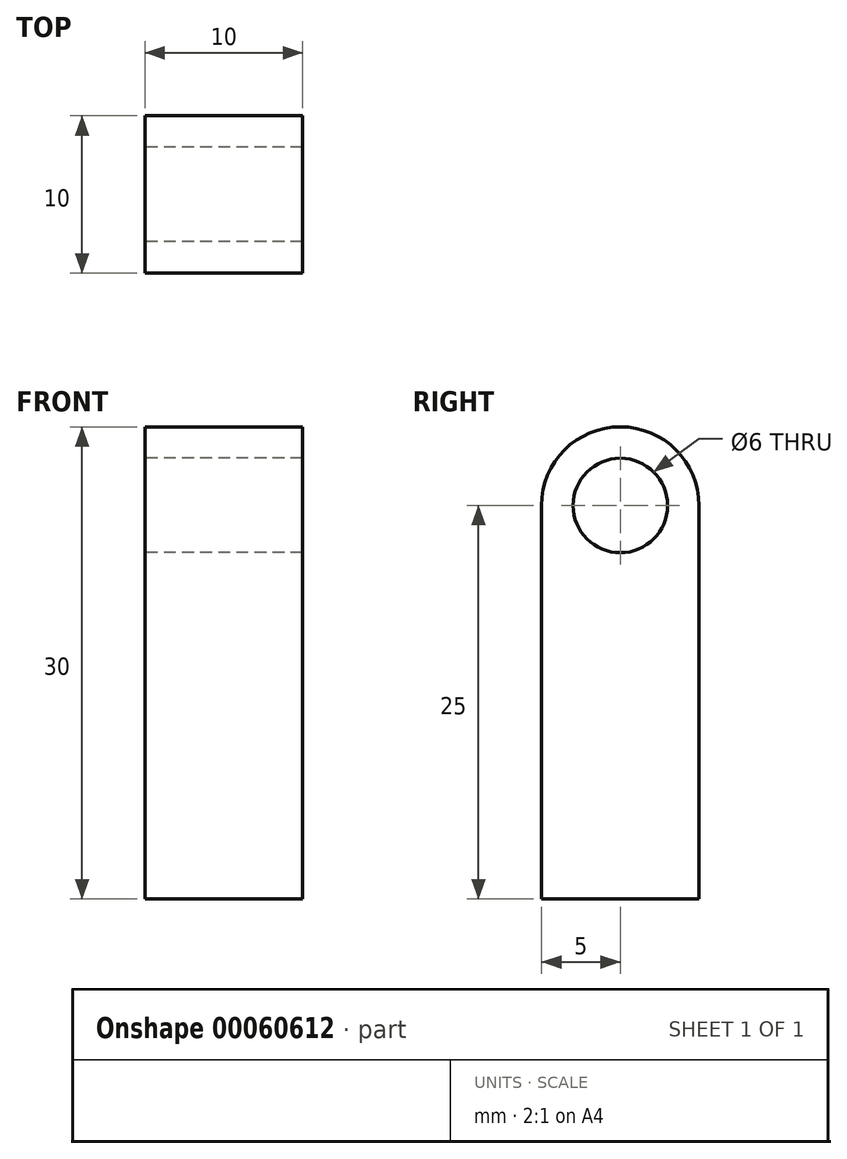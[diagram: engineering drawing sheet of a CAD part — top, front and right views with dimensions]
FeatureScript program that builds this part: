
annotation { "Feature Type Name" : "Feature", "Feature Type Description" : "" }
export const myFeature = defineFeature(function(context is Context, id is Id, definition is map)
    precondition{}
    {
        {
            var Q0;
            Q0=qCreatedBy(makeId("Top.planeOp"),FACE);
            var sketch = newSketch(context, id + "F0", { "sketchPlane" : qUnion([Q0])});
            skLineSegment(sketch, "E0.rect.bottom", {"start": v(-5, 5) * mm, "end": v(5, 5) * mm});
            skLineSegment(sketch, "E0.rect.top", {"start": v(-5, -5) * mm, "end": v(5, -5) * mm});
            skLineSegment(sketch, "E0.rect.left", {"start": v(-5, 5) * mm, "end": v(-5, -5) * mm});
            skLineSegment(sketch, "E0.rect.right", {"start": v(5, 5) * mm, "end": v(5, -5) * mm});
            skPoint(sketch, "E0.rect.middle", {"position": v(0, 0) * mm});
            skSolve(sketch);
        }
        {
            var Q0;
            Q0=makeQuery(id+"F0.imprint","IMPRINT",FACE,{"disambiguationData":[TD([[makeQuery(id+"F0.imprint","IMPRINT",EDGE,{"derivedFrom":sQuery(id+"F0.wireOp",EDGE,"E0.rect.bottom")}),-1.0]])]});
            extrude(context, id + "F1", {"entities" : qUnion([Q0]), "depth" : 20 * mm});
        }
        {
            var Q0;
            Q0=makeQuery(id+"F1.opExtrude","CAP_FACE",FACE,{"disambiguationData":[OSD([sQuery(id+"F0.wireOp",EDGE,"E0.rect.bottom"),sQuery(id+"F0.wireOp",EDGE,"E0.rect.top"),sQuery(id+"F0.wireOp",EDGE,"E0.rect.left"),sQuery(id+"F0.wireOp",EDGE,"E0.rect.right")])],"isStart":false});
            var sketch = newSketch(context, id + "F2", { "sketchPlane" : qUnion([Q0])});
            skLineSegment(sketch, "E1.rect.bottom", {"start": v(-7, 5) * mm, "end": v(7, 5) * mm});
            skLineSegment(sketch, "E1.rect.top", {"start": v(-7, -5) * mm, "end": v(7, -5) * mm});
            skLineSegment(sketch, "E1.rect.left", {"start": v(-7, 5) * mm, "end": v(-7, -5) * mm});
            skLineSegment(sketch, "E1.rect.right", {"start": v(7, 5) * mm, "end": v(7, -5) * mm});
            skPoint(sketch, "E1.rect.middle", {"position": v(0, 0) * mm});
            skSolve(sketch);
        }
        {
            var Q0;
            {var subQ2=sQuery(id+"F2.wireOp",EDGE,"E1.rect.left");Q0=makeQuery(id+"F2.imprint","IMPRINT",FACE,{"disambiguationData":[TD([[makeQuery(id+"F2.imprint","IMPRINT",EDGE,{"derivedFrom":subQ2}),1.0]])]});}
            var Q1;
            {var subQ1=makeQuery(id+"F1.opExtrude","CAP_EDGE",EDGE,{"disambiguationData":[OSD([sQuery(id+"F0.wireOp",EDGE,"E0.rect.left")])],"isStart":false});Q1=makeQuery(id+"F2.imprint","IMPRINT",FACE,{"disambiguationData":[TD([[makeQuery(id+"F2.imprint","IMPRINT",EDGE,{"derivedFrom":subQ1}),1.0]])]});}
            var Q2;
            {var subQ2=sQuery(id+"F2.wireOp",EDGE,"E1.rect.right");Q2=makeQuery(id+"F2.imprint","IMPRINT",FACE,{"disambiguationData":[TD([[makeQuery(id+"F2.imprint","IMPRINT",EDGE,{"derivedFrom":subQ2}),-1.0]])]});}
            extrude(context, id + "F3", {"entities" : qUnion([Q0, Q1, Q2]), "operationType" : NewBodyOperationType.ADD, "depth" : 10 * mm});
        }
        {
            var Q0;
            Q0=makeQuery(id+"F3.opExtrude","SWEPT_FACE",FACE,{"disambiguationData":[OSD([sQuery(id+"F2.wireOp",EDGE,"E1.rect.left")])]});
            var sketch = newSketch(context, id + "F4", { "sketchPlane" : qUnion([Q0])});
            skCircle(sketch, "E2", {"center": v(0, 25) * mm, "radius": 3 * mm});
            skSolve(sketch);
        }
        {
            var Q0;
            Q0=makeQuery(id+"F3.opExtrude","SWEPT_FACE",FACE,{"disambiguationData":[OSD([sQuery(id+"F2.wireOp",EDGE,"E1.rect.right")])]});
            var sketch = newSketch(context, id + "F5", { "sketchPlane" : qUnion([Q0])});
            skCircle(sketch, "E3", {"center": v(0, 25) * mm, "radius": 3 * mm});
            skSolve(sketch);
        }
        {
            var Q0;
            {var subQ0=sQuery(id+"F2.wireOp",EDGE,"E1.rect.left");var subQ1=sQuery(id+"F2.wireOp",EDGE,"E1.rect.bottom");Q0=makeQuery(id+"FH2xxagkPyGd56d_1.boolean.opBoolean","SPLIT",EDGE,{"disambiguationData":[TD([makeQuery(id+"F3.opExtrude","SWEPT_FACE",FACE,{"disambiguationData":[OSD([subQ0])]})])],"derivedFrom":makeQuery(id+"F3.opExtrude","CAP_EDGE",EDGE,{"disambiguationData":[OSD([subQ1])],"isStart":false})});}
            var Q1;
            {var subQ0=sQuery(id+"F2.wireOp",EDGE,"E1.rect.right");var subQ1=sQuery(id+"F2.wireOp",EDGE,"E1.rect.bottom");Q1=makeQuery(id+"FH2xxagkPyGd56d_1.boolean.opBoolean","SPLIT",EDGE,{"disambiguationData":[TD([makeQuery(id+"F3.opExtrude","SWEPT_FACE",FACE,{"disambiguationData":[OSD([subQ0])]})])],"derivedFrom":makeQuery(id+"F3.opExtrude","CAP_EDGE",EDGE,{"disambiguationData":[OSD([subQ1])],"isStart":false})});}
            var Q2;
            {var subQ0=sQuery(id+"F2.wireOp",EDGE,"E1.rect.right");var subQ1=sQuery(id+"F2.wireOp",EDGE,"E1.rect.top");Q2=makeQuery(id+"FH2xxagkPyGd56d_1.boolean.opBoolean","SPLIT",EDGE,{"disambiguationData":[TD([makeQuery(id+"F3.opExtrude","SWEPT_FACE",FACE,{"disambiguationData":[OSD([subQ0])]})])],"derivedFrom":makeQuery(id+"F3.opExtrude","CAP_EDGE",EDGE,{"disambiguationData":[OSD([subQ1])],"isStart":false})});}
            var Q3;
            {var subQ0=sQuery(id+"F2.wireOp",EDGE,"E1.rect.left");var subQ1=sQuery(id+"F2.wireOp",EDGE,"E1.rect.top");Q3=makeQuery(id+"FH2xxagkPyGd56d_1.boolean.opBoolean","SPLIT",EDGE,{"disambiguationData":[TD([makeQuery(id+"F3.opExtrude","SWEPT_FACE",FACE,{"disambiguationData":[OSD([subQ0])]})])],"derivedFrom":makeQuery(id+"F3.opExtrude","CAP_EDGE",EDGE,{"disambiguationData":[OSD([subQ1])],"isStart":false})});}
            fillet(context, id + "F6", {"entities" : qUnion([Q0, Q1, Q2, Q3]), "radius" : 5 * mm, "tangentPropagation" : true, "allowEdgeOverflow" : false});
        }
        {
            var Q0;
            Q0=makeQuery(id+"F5.imprint","IMPRINT",FACE,{"disambiguationData":[TD([[makeQuery(id+"F5.imprint","IMPRINT",EDGE,{"derivedFrom":sQuery(id+"F5.wireOp",EDGE,"E3")}),-1.0]])]});
            extrude(context, id + "F7", {"entities" : qUnion([Q0]), "operationType" : NewBodyOperationType.REMOVE, "oppositeDirection" : true, "depth" : 2 * mm});
        }
        {
            var Q0;
            Q0=makeQuery(id+"F4.imprint","IMPRINT",FACE,{"disambiguationData":[TD([[makeQuery(id+"F4.imprint","IMPRINT",EDGE,{"derivedFrom":sQuery(id+"F4.wireOp",EDGE,"E2")}),-1.0]])]});
            extrude(context, id + "F8", {"entities" : qUnion([Q0]), "operationType" : NewBodyOperationType.REMOVE, "oppositeDirection" : true, "depth" : 2 * mm});
        }
        {
            var Q0;
            Q0=makeQuery(id+"F3.opExtrude","SWEPT_FACE",FACE,{"disambiguationData":[OSD([sQuery(id+"F2.wireOp",EDGE,"E1.rect.left")])]});
            extrude(context, id + "F9", {"entities" : qUnion([Q0]), "operationType" : NewBodyOperationType.REMOVE, "endBound" : BoundingType.THROUGH_ALL, "oppositeDirection" : true, "depth" : 25 * mm});
        }
    });
